# Revit family: NBS_WallgateLtd_Shlvs_ALF
name_source: partatom
category: Furniture Systems
revit_build: Autodesk Revit 2014 (Build: 20130709_2115(x64)
units: mm (PartAtom-declared; Revit-internal decimal feet)

## types (2) — shared parameters
AssetType = Fixed
Certification = Ministry of Justice Safer Cell Approval
ColourOptions = MA - Thames, MAH - Frost, MAW - White, MC - Bluestone, MCA - Aubergine, MCB - Diamantina, MCC - Black, MCD - Orange, MCE - Pink, MO - Slate, MS - Hyco, MCJ - Light Grey, MCF - NHS Blue
Description = Anti-Ligature, anti-vandal solid surface shelf
Durability = Compliant to Grade 5
DurationUnit = year
Features = Hygienic and easily cleaned, highly vandal-resistant
Finish = Solid Surface
FixingMaterial = NBS_Concept
FixingOffset = 50 mm  [stored 0.164042 ft]
FormOptions = Through wall fixings or security screws
IfcExportAs = IfcFurnitureType
IfcExportType = SHELF
ManufacturerName = Wallgate Ltd
ManufacturerURL = www.wallgate.com
Material = High-grade solid surface material
MaximumWallThickness = 170 mm  [stored 0.557743 ft]
NBSCertification = www.nationalbimlibrary.com/cert/ne2gtbre
NBSDescription = Shelves
NBSReference = 45-35-72/354
NominalDepth = 100 mm  [stored 0.328084 ft]
NominalHeight = 125 mm  [stored 0.410105 ft]
ProductInformation = www.wallgate.com/products/washroom-accessories/alf-anti-ligature-shelves-range
ShelfDepth = 100 mm  [stored 0.328084 ft]
ShelfHeight = 125 mm  [stored 0.410105 ft]
ShelfMaterial = NBS_Concept
Uniclass2 = 45-31-78/406
Version = 1
WarrantyDurationUnit = year
zero-valued in all types: NominalWidth

## per-type parameters (varying)
| type | BIMObjectName | CentralFixing | Name | NominalLength | ShelfLength | Size | WarrantyDurationParts | Weight |
| ALF-01 | NBS_WallgateLtd_Shelves_ALF-01 | Yes | Shelves_ALF-01_WallgateLtd | 470 mm  [stored 1.54199 ft] | 470 mm  [stored 1.54199 ft] | 470 x 125 x 100 mm | 1 | 4.25 kg |
| ALF-02 | NBS_WallgateLtd_Shelves_ALF-02 | No | Shelves_ALF-02_WallgateLtd | 235 mm  [stored 0.770997 ft] | 235 mm  [stored 0.770997 ft] | 235 x 125 x 100 mm |  | 2.9 kg |

note: column(s) folded — value = type name in every type: ModelNumber

note: [stored X ft] marks values corroborated as IEEE doubles in the binary element streams (Revit-internal decimal feet)

## geometry (parser evidence)
native form markers: Sweep x1
no freeform markers — native parametric forms only
